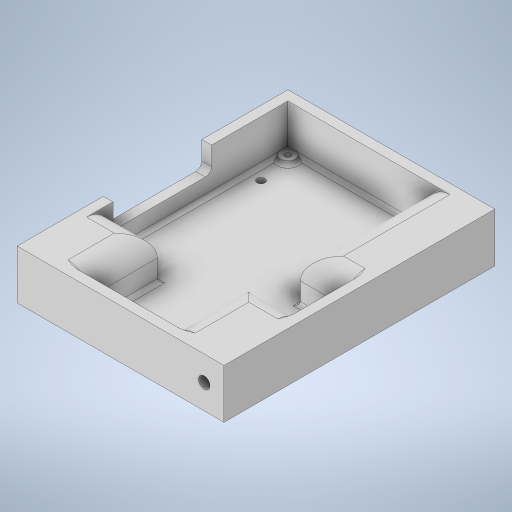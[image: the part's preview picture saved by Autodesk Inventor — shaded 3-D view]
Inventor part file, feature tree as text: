
AUTODESK INVENTOR PART (.ipt)
format: ipt  version: 2024 (Build 280153000, 153)  size: 1,590,784 bytes
history: native  units: in
note: dims shown in document units (in); Inventor stores cm internally (conversion verified against a paired STEP export)
features: extrude x8, sketch x7, fillet x5, projected_geometry x5, mirror x3, plane x2, emboss x1
ambient origin geometry x8: Origin, YZ Plane, XZ Plane, XY Plane, X Axis, Y Axis, Z Axis, Center Point
bodies: Solid1 (feature_tree)
feature tree (31):
  sketch  "Sketch1"  dims[d2=0.2in d3=0.0in d4=0.3in]
  extrude  "Extrusion5"  Depth=0.3in
  extrude  "Extrusion2"  Depth=0.3in
  extrude  "Extrusion4"  Depth=0.125in
  fillet  "Fillet1"  Radius=0.125in
  fillet  "Fillet2"  Radius=0.125in
  fillet  "Fillet3"  Radius=0.125in
  fillet  "Fillet4"  Radius=2.76in
  emboss  "Emboss1"
  extrude  "Extrusion8"  Depth=3.348in
  extrude  "Extrusion9"  Depth=1.0in
  fillet  "Fillet5"  Radius=1.0in
  extrude  "Extrusion10"  Depth=1.0in
  plane  "Work Plane1"
  plane  "Work Plane2"
  mirror  "Mirror4"
  extrude  "Extrusion6"  Depth=0.125in TaperAngle=0.0deg
  mirror  "Mirror1"
  extrude  "Extrusion7"  Depth=0.4331in
  mirror  "Mirror3"
  sketch  "Sketch2"  dims[d5=0.3in d6=0.3in]
  projected_geometry  "Projected Loop1"
  sketch  "Sketch3"  dims[d7=0.3in d8=0.125in d9=0.125in d10=0.125in d11=0.125in d18=2.76in]
  projected_geometry  "Projected Loop2"
  sketch  "Sketch4"  dims[d19=3.55in d23=3.348in]
  sketch  "Sketch5"  dims[d24=2.555in d25=1.5in d26=1.0in]
  projected_geometry  "Projected Loop3"
  sketch  "Sketch6"  dims[d31=1.0in d32=1.0in]
  projected_geometry  "Projected Loop4"
  sketch  "Sketch7"  dims[d33=1.0in d34=0.0in d35=0.125in d36=0.0in d37=0.4375in d38=0.4375in d39=0.4375in d40=0.075in d41=5.5in d43=4.2in d45=0.1in d46=0.3in d49=0.125in d50=0.0in d51=0.1in d53=0.1in d54=0.2362in d55=0.4in d56=0.4331in d57=0.0in d58=0.0157in d59=0.0in d60=0.16in d61=0.2362in d62=1.0in d63=0.45in d64=1.0in d65=0.45in d66=0.4331in d67=0.0in d68=2.0in d69=0.5in d70=1.0in d71=0.0in d72=0.125in d73=0.2362in d74=0.4in d75=0.4331in d76=0.0in]
  projected_geometry  "Projected Loop5"
